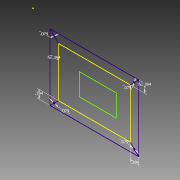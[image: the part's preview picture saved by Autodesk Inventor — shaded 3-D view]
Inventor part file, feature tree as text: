
AUTODESK INVENTOR PART (.ipt)
format: ipt  version: 2015 (Build 190159000, 159)  size: 74,752 bytes
history: native  units: in
note: dims shown in document units (in); Inventor stores cm internally (conversion verified against a paired STEP export)
features: reference x4, sketch x1
ambient origin geometry x8: Origin, YZ Plane, XZ Plane, XY Plane, X Axis, Y Axis, Z Axis, Center Point
feature tree (5):
  sketch  "Sketch1"  dims[d0=0.3937in d1=0.3937in d2=0.3937in d3=0.3937in d4=0.0787in d5=0.0787in d6=0.0787in d7=0.0787in]
  reference  "Reference1"
  reference  "Reference2"
  reference  "Reference3"
  reference  "Reference4"
